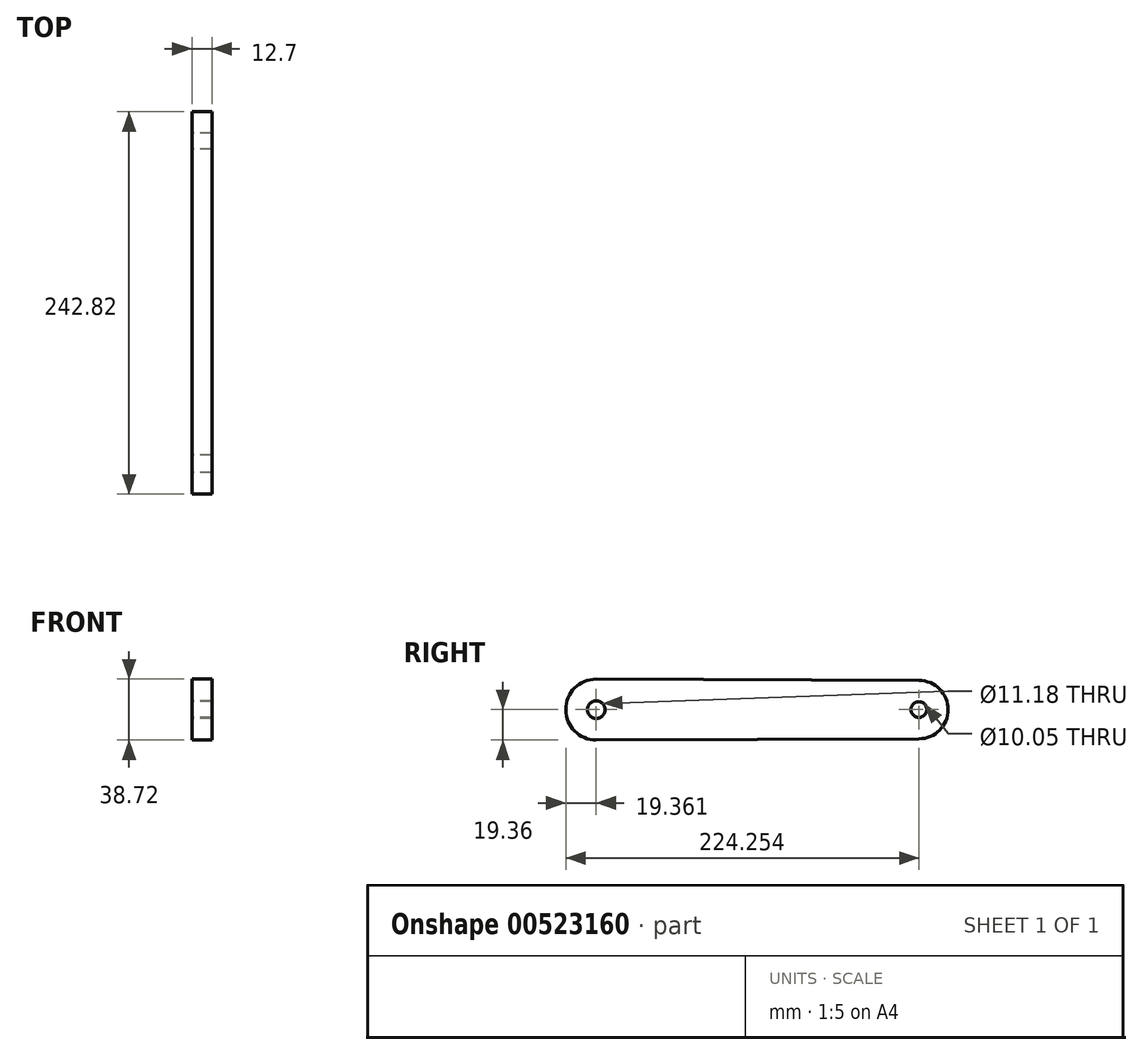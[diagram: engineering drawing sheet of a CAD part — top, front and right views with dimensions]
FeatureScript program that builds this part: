
annotation { "Feature Type Name" : "Feature", "Feature Type Description" : "" }
export const myFeature = defineFeature(function(context is Context, id is Id, definition is map)
    precondition{}
    {
        {
            var Q0;
            Q0=qCreatedBy(makeId("Right.planeOp"),FACE);
            var sketch = newSketch(context, id + "F0", { "sketchPlane" : qUnion([Q0])});
            skLineSegment(sketch, "E0", {"start": v(0, 0) * mm, "end": v(99.72, 0) * mm, "construction": true});
            skLineSegment(sketch, "E1", {"start": v(0, 0) * mm, "end": v(-105.17, 0) * mm, "construction": true});
            skCircle(sketch, "E2", {"center": v(99.72, 0) * mm, "radius": 18.56 * mm});
            skCircle(sketch, "E3", {"center": v(-105.17, 0) * mm, "radius": 19.36 * mm});
            skCircle(sketch, "E4", {"center": v(-105.17, 0) * mm, "radius": 5.59 * mm});
            skCircle(sketch, "E5", {"center": v(99.72, 0) * mm, "radius": 5.02 * mm});
            skLineSegment(sketch, "E6", {"start": v(-105.17, 19.36) * mm, "end": v(99.8, 18.56) * mm});
            skLineSegment(sketch, "E7", {"start": v(-105.17, -19.36) * mm, "end": v(102.87, -18.55) * mm});
            skSolve(sketch);
        }
        {
            var Q0;
            Q0=makeQuery(id+"F0.imprint","IMPRINT",FACE,{"disambiguationData":[TD([[makeQuery(id+"F0.imprint","IMPRINT",EDGE,{"derivedFrom":sQuery(id+"F0.wireOp",EDGE,"E4")}),-1.0]])]});
            var Q1;
            {var subQ0=sQuery(id+"F0.wireOp",EDGE,"E6");Q1=makeQuery(id+"F0.imprint","IMPRINT",FACE,{"disambiguationData":[TD([[makeQuery(id+"F0.imprint","IMPRINT",EDGE,{"derivedFrom":subQ0}),-1.0]])]});}
            var Q2;
            Q2=makeQuery(id+"F0.imprint","IMPRINT",FACE,{"disambiguationData":[TD([[makeQuery(id+"F0.imprint","IMPRINT",EDGE,{"derivedFrom":sQuery(id+"F0.wireOp",EDGE,"E5")}),-1.0]])]});
            extrude(context, id + "F1", {"entities" : qUnion([Q0, Q1, Q2]), "depth" : 12.7 * mm, "offsetDistance" : 25.4 * mm});
        }
    });
